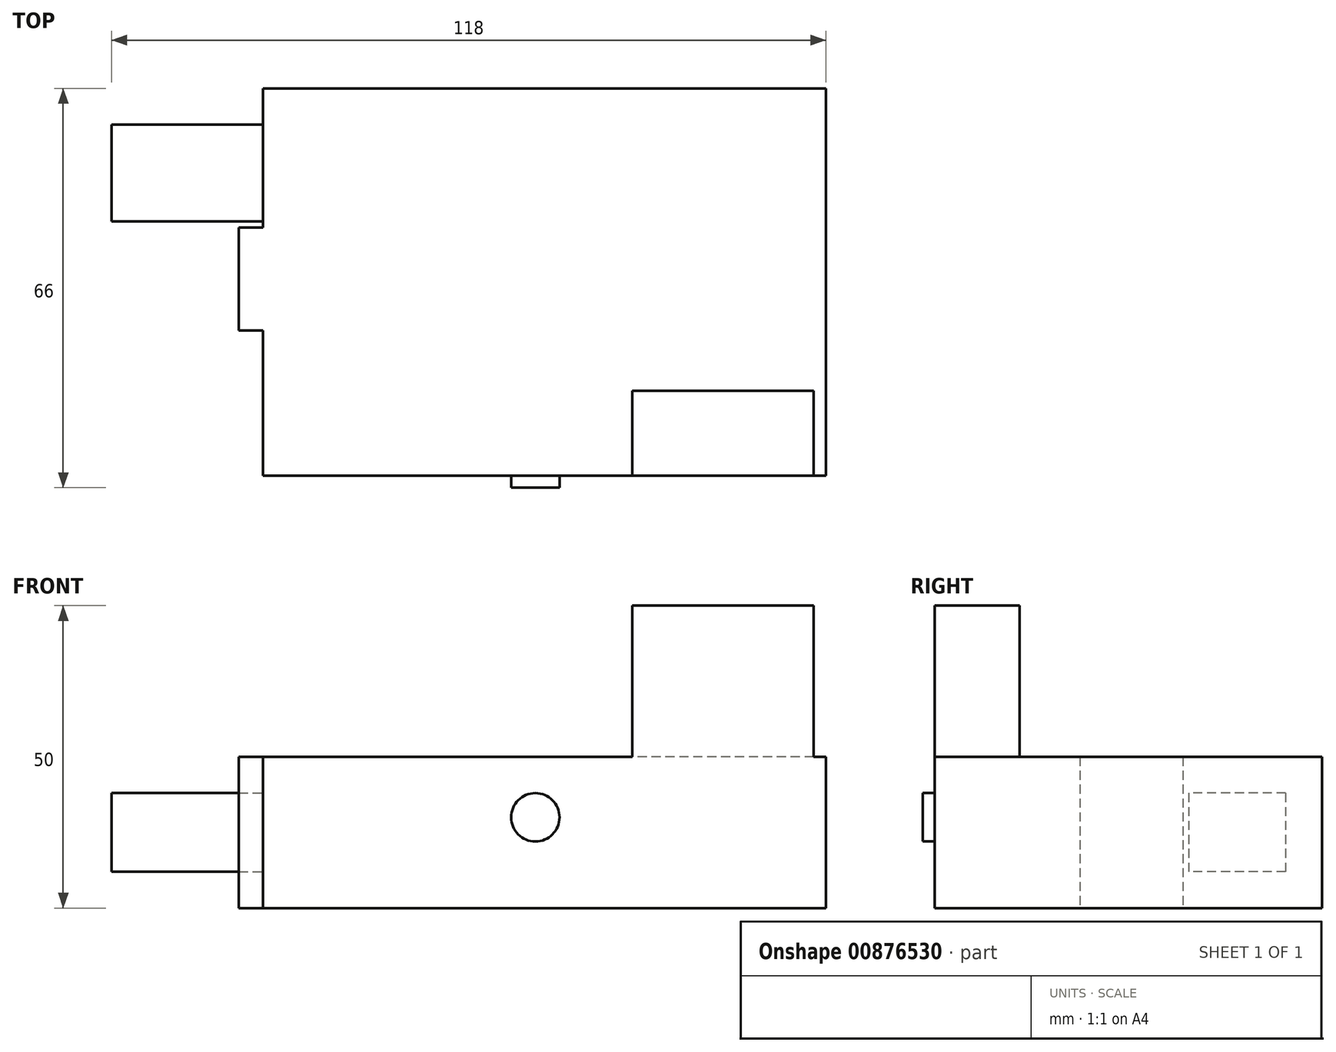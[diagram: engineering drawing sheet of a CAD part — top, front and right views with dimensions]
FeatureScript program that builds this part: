
annotation { "Feature Type Name" : "Feature", "Feature Type Description" : "" }
export const myFeature = defineFeature(function(context is Context, id is Id, definition is map)
    precondition{}
    {
        {
            var Q0;
            Q0=qCreatedBy(makeId("Top.planeOp"),FACE);
            var sketch = newSketch(context, id + "F0", { "sketchPlane" : qUnion([Q0])});
            skLineSegment(sketch, "E0.left", {"start": v(46.56, -32) * mm, "end": v(46.56, 32) * mm});
            skPoint(sketch, "E0.middle", {"position": v(-1.94, 0) * mm});
            skLineSegment(sketch, "E1.top", {"start": v(-50.44, -8) * mm, "end": v(-46.44, -8) * mm});
            skLineSegment(sketch, "E1.right", {"start": v(-46.44, -32) * mm, "end": v(-46.44, -8) * mm});
            skLineSegment(sketch, "E2", {"start": v(-46.44, -8) * mm, "end": v(-46.44, 9) * mm});
            skLineSegment(sketch, "E3", {"start": v(-46.44, 9) * mm, "end": v(-50.44, 9) * mm});
            skLineSegment(sketch, "E4", {"start": v(-50.44, 9) * mm, "end": v(-50.44, -8) * mm});
            skLineSegment(sketch, "E5", {"start": v(-46.44, 9) * mm, "end": v(-46.44, 32) * mm});
            skLineSegment(sketch, "E6", {"start": v(-46.44, 32) * mm, "end": v(46.56, 32) * mm});
            skLineSegment(sketch, "E7", {"start": v(-46.44, -32) * mm, "end": v(46.56, -32) * mm});
            skSolve(sketch);
        }
        {
            var Q0;
            Q0 = qSketchRegion(id + "F0", true);
            extrude(context, id + "F1", {"entities" : qUnion([Q0]), "depth" : 25 * mm, "offsetDistance" : 25 * mm});
        }
        {
            var Q0;
            Q0=makeQuery(id+"F1.opExtrude","SWEPT_FACE",FACE,{"disambiguationData":[OSD([sQuery(id+"F0.wireOp",EDGE,"E7")])]});
            var sketch = newSketch(context, id + "F2", { "sketchPlane" : qUnion([Q0])});
            skCircle(sketch, "E8", {"center": v(-1.44, 15) * mm, "radius": 4 * mm});
            skSolve(sketch);
        }
        {
            var Q0;
            Q0=makeQuery(id+"F2.imprint","IMPRINT",FACE,{"disambiguationData":[TD([[makeQuery(id+"F2.imprint","IMPRINT",EDGE,{"derivedFrom":sQuery(id+"F2.wireOp",EDGE,"E8")}),1.0]])]});
            extrude(context, id + "F3", {"entities" : qUnion([Q0]), "operationType" : NewBodyOperationType.ADD, "depth" : 2 * mm, "offsetDistance" : 25 * mm});
        }
        {
            var Q0;
            Q0=makeQuery(id+"F1.opExtrude","CAP_FACE",FACE,{"disambiguationData":[OSD([sQuery(id+"F0.wireOp",EDGE,"E0.left"),sQuery(id+"F0.wireOp",EDGE,"E1.top"),sQuery(id+"F0.wireOp",EDGE,"E1.right"),sQuery(id+"F0.wireOp",EDGE,"E3"),sQuery(id+"F0.wireOp",EDGE,"E4"),sQuery(id+"F0.wireOp",EDGE,"E5"),sQuery(id+"F0.wireOp",EDGE,"E6"),sQuery(id+"F0.wireOp",EDGE,"E7")])],"isStart":false});
            var sketch = newSketch(context, id + "F4", { "sketchPlane" : qUnion([Q0])});
            skLineSegment(sketch, "E9.bottom", {"start": v(46.56, -32) * mm, "end": v(44.56, -32) * mm});
            skLineSegment(sketch, "E9.top", {"start": v(46.56, -18) * mm, "end": v(44.56, -18) * mm});
            skLineSegment(sketch, "E9.left", {"start": v(46.56, -32) * mm, "end": v(46.56, -18) * mm});
            skLineSegment(sketch, "E9.right", {"start": v(44.56, -32) * mm, "end": v(44.56, -18) * mm});
            skLineSegment(sketch, "E10.bottom", {"start": v(44.56, -18) * mm, "end": v(14.56, -18) * mm});
            skLineSegment(sketch, "E10.top", {"start": v(44.56, -32) * mm, "end": v(14.56, -32) * mm});
            skLineSegment(sketch, "E10.left", {"start": v(44.56, -18) * mm, "end": v(44.56, -32) * mm});
            skLineSegment(sketch, "E10.right", {"start": v(14.56, -18) * mm, "end": v(14.56, -32) * mm});
            skSolve(sketch);
        }
        {
            var Q0;
            Q0=makeQuery(id+"F4.imprint","IMPRINT",FACE,{"disambiguationData":[TD([[makeQuery(id+"F4.imprint","IMPRINT",EDGE,{"derivedFrom":sQuery(id+"F4.wireOp",EDGE,"E10.bottom")}),1.0]])]});
            extrude(context, id + "F5", {"entities" : qUnion([Q0]), "operationType" : NewBodyOperationType.ADD, "depth" : 25 * mm, "offsetDistance" : 25 * mm});
        }
        {
            var Q0;
            Q0=makeQuery(id+"F1.opExtrude","SWEPT_FACE",FACE,{"disambiguationData":[OSD([sQuery(id+"F0.wireOp",EDGE,"E5")])]});
            var sketch = newSketch(context, id + "F6", { "sketchPlane" : qUnion([Q0])});
            skLineSegment(sketch, "E11.bottom", {"start": v(-26, 19) * mm, "end": v(-10, 19) * mm});
            skLineSegment(sketch, "E11.top", {"start": v(-26, 6) * mm, "end": v(-10, 6) * mm});
            skLineSegment(sketch, "E11.left", {"start": v(-26, 19) * mm, "end": v(-26, 6) * mm});
            skLineSegment(sketch, "E11.right", {"start": v(-10, 19) * mm, "end": v(-10, 6) * mm});
            skSolve(sketch);
        }
        {
            var Q0;
            Q0=makeQuery(id+"F6.imprint","IMPRINT",FACE,{"disambiguationData":[TD([[makeQuery(id+"F6.imprint","IMPRINT",EDGE,{"derivedFrom":sQuery(id+"F6.wireOp",EDGE,"E11.bottom")}),-1.0]])]});
            extrude(context, id + "F7", {"entities" : qUnion([Q0]), "operationType" : NewBodyOperationType.ADD, "depth" : 25 * mm, "offsetDistance" : 25 * mm});
        }
    });
